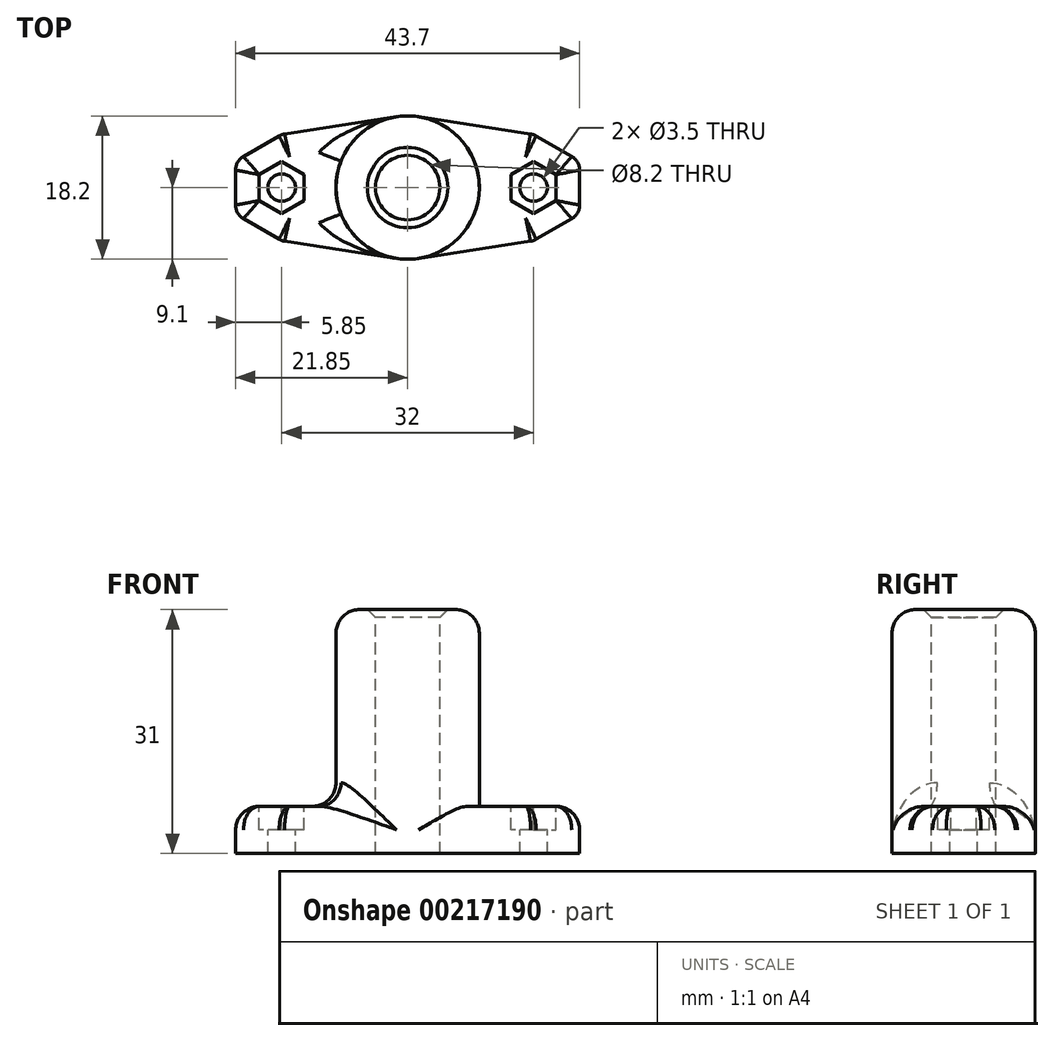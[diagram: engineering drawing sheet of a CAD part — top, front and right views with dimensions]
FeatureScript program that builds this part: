
annotation { "Feature Type Name" : "Feature", "Feature Type Description" : "" }
export const myFeature = defineFeature(function(context is Context, id is Id, definition is map)
    precondition{}
    {
        {
            var Q0;
            Q0=qCreatedBy(makeId("Top.planeOp"),FACE);
            var sketch = newSketch(context, id + "F0", { "sketchPlane" : qUnion([Q0])});
            skCircle(sketch, "E0", {"center": v(0, 0) * mm, "radius": 4.1 * mm});
            skCircle(sketch, "E1", {"center": v(-16, 0) * mm, "radius": 1.75 * mm});
            skCircle(sketch, "E2.cCircle", {"center": v(-16, 0) * mm, "radius": 2.85 * mm, "construction": true});
            skLineSegment(sketch, "E2.0", {"start": v(-18.85, -1.65) * mm, "end": v(-18.85, 1.65) * mm});
            skLineSegment(sketch, "E2.1", {"start": v(-18.85, 1.65) * mm, "end": v(-16, 3.3) * mm});
            skLineSegment(sketch, "E2.2", {"start": v(-16, 3.3) * mm, "end": v(-13.15, 1.65) * mm});
            skLineSegment(sketch, "E2.3", {"start": v(-13.15, 1.65) * mm, "end": v(-13.15, -1.65) * mm});
            skLineSegment(sketch, "E2.4", {"start": v(-13.15, -1.65) * mm, "end": v(-16, -3.3) * mm});
            skLineSegment(sketch, "E2.5", {"start": v(-16, -3.3) * mm, "end": v(-18.85, -1.65) * mm});
            skPoint(sketch, "E2.0.midPoint", {"position": v(-18.85, 0) * mm});
            skCircle(sketch, "E3.0", {"center": v(0, 0) * mm, "radius": 9.1 * mm});
            skCircle(sketch, "E4.cCircle", {"center": v(-16, 0) * mm, "radius": 5.85 * mm, "construction": true});
            skLineSegment(sketch, "E4.0", {"start": v(-21.85, -3.38) * mm, "end": v(-21.85, 3.38) * mm});
            skLineSegment(sketch, "E4.1", {"start": v(-21.85, 3.38) * mm, "end": v(-16, 6.75) * mm});
            skLineSegment(sketch, "E4.2", {"start": v(-16, 6.75) * mm, "end": v(-10.15, 3.38) * mm});
            skLineSegment(sketch, "E4.3", {"start": v(-10.15, 3.38) * mm, "end": v(-10.15, -3.38) * mm});
            skLineSegment(sketch, "E4.4", {"start": v(-10.15, -3.38) * mm, "end": v(-16, -6.75) * mm});
            skLineSegment(sketch, "E4.5", {"start": v(-16, -6.75) * mm, "end": v(-21.85, -3.38) * mm});
            skPoint(sketch, "E4.0.midPoint", {"position": v(-21.85, 0) * mm});
            skLineSegment(sketch, "E5.MirrorCS", {"start": v(10.15, -3.38) * mm, "end": v(16, -6.75) * mm});
            skPoint(sketch, "E6.MirrorP", {"position": v(18.85, 0) * mm});
            skLineSegment(sketch, "E7.MirrorCS", {"start": v(13.15, 1.65) * mm, "end": v(13.15, -1.65) * mm});
            skLineSegment(sketch, "E8.MirrorCS", {"start": v(16, -3.3) * mm, "end": v(18.85, -1.65) * mm});
            skLineSegment(sketch, "E9.MirrorCS", {"start": v(16, -6.75) * mm, "end": v(21.85, -3.38) * mm});
            skLineSegment(sketch, "E10.MirrorCS", {"start": v(16, 6.75) * mm, "end": v(10.15, 3.38) * mm});
            skCircle(sketch, "E11.MirrorC", {"center": v(16, 0) * mm, "radius": 1.75 * mm});
            skLineSegment(sketch, "E12.MirrorCS", {"start": v(21.85, 3.38) * mm, "end": v(16, 6.75) * mm});
            skLineSegment(sketch, "E13.MirrorCS", {"start": v(10.15, 3.38) * mm, "end": v(10.15, -3.38) * mm});
            skLineSegment(sketch, "E14.MirrorCS", {"start": v(21.85, -3.38) * mm, "end": v(21.85, 3.38) * mm});
            skCircle(sketch, "E15.MirrorC", {"center": v(16, 0) * mm, "radius": 5.85 * mm, "construction": true});
            skLineSegment(sketch, "E16.MirrorCS", {"start": v(13.15, -1.65) * mm, "end": v(16, -3.3) * mm});
            skLineSegment(sketch, "E17.MirrorCS", {"start": v(18.85, 1.65) * mm, "end": v(16, 3.3) * mm});
            skCircle(sketch, "E18.MirrorC", {"center": v(16, 0) * mm, "radius": 2.85 * mm, "construction": true});
            skLineSegment(sketch, "E19.MirrorCS", {"start": v(16, 3.3) * mm, "end": v(13.15, 1.65) * mm});
            skLineSegment(sketch, "E20.MirrorCS", {"start": v(18.85, -1.65) * mm, "end": v(18.85, 1.65) * mm});
            skPoint(sketch, "E21.MirrorP", {"position": v(21.85, 0) * mm});
            skLineSegment(sketch, "E22", {"start": v(-16, 6.75) * mm, "end": v(-1.38, 9) * mm});
            skLineSegment(sketch, "E23", {"start": v(16, 6.75) * mm, "end": v(1.38, 9) * mm});
            skLineSegment(sketch, "E24", {"start": v(16, -6.75) * mm, "end": v(1.38, -9) * mm});
            skLineSegment(sketch, "E25", {"start": v(-16, -6.75) * mm, "end": v(-1.38, -9) * mm});
            skSolve(sketch);
        }
        {
            var Q0;
            Q0=makeQuery(id+"F0.imprint","IMPRINT",FACE,{"disambiguationData":[TD([[makeQuery(id+"F0.imprint","IMPRINT",EDGE,{"derivedFrom":sQuery(id+"F0.wireOp",EDGE,"E2.0")}),1.0]])]});
            var Q1;
            Q1=makeQuery(id+"F0.imprint","IMPRINT",FACE,{"disambiguationData":[TD([[makeQuery(id+"F0.imprint","IMPRINT",EDGE,{"derivedFrom":sQuery(id+"F0.wireOp",EDGE,"E1")}),-1.0]])]});
            var Q2;
            Q2=makeQuery(id+"F0.imprint","IMPRINT",FACE,{"disambiguationData":[TD([[makeQuery(id+"F0.imprint","IMPRINT",EDGE,{"derivedFrom":sQuery(id+"F0.wireOp",EDGE,"E4.2")}),1.0]])]});
            var Q3;
            Q3=makeQuery(id+"F0.imprint","IMPRINT",FACE,{"disambiguationData":[TD([[makeQuery(id+"F0.imprint","IMPRINT",EDGE,{"derivedFrom":sQuery(id+"F0.wireOp",EDGE,"E0")}),-1.0]])]});
            var Q4;
            Q4=makeQuery(id+"F0.imprint","IMPRINT",FACE,{"disambiguationData":[TD([[makeQuery(id+"F0.imprint","IMPRINT",EDGE,{"derivedFrom":sQuery(id+"F0.wireOp",EDGE,"E5.MirrorCS")}),-1.0]])]});
            var Q5;
            Q5=makeQuery(id+"F0.imprint","IMPRINT",FACE,{"disambiguationData":[TD([[makeQuery(id+"F0.imprint","IMPRINT",EDGE,{"derivedFrom":sQuery(id+"F0.wireOp",EDGE,"E5.MirrorCS")}),1.0]])]});
            var Q6;
            Q6=makeQuery(id+"F0.imprint","IMPRINT",FACE,{"disambiguationData":[TD([[makeQuery(id+"F0.imprint","IMPRINT",EDGE,{"derivedFrom":sQuery(id+"F0.wireOp",EDGE,"E7.MirrorCS")}),1.0]])]});
            extrude(context, id + "F1", {"entities" : qUnion([Q0, Q1, Q2, Q3, Q4, Q5, Q6]), "oppositeDirection" : true, "depth" : 6 * mm});
        }
        {
            var Q0;
            Q0=makeQuery(id+"F0.imprint","IMPRINT",FACE,{"disambiguationData":[TD([[makeQuery(id+"F0.imprint","IMPRINT",EDGE,{"derivedFrom":sQuery(id+"F0.wireOp",EDGE,"E1")}),-1.0]])]});
            var Q1;
            Q1=makeQuery(id+"F0.imprint","IMPRINT",FACE,{"disambiguationData":[TD([[makeQuery(id+"F0.imprint","IMPRINT",EDGE,{"derivedFrom":sQuery(id+"F0.wireOp",EDGE,"E7.MirrorCS")}),1.0]])]});
            extrude(context, id + "F2", {"entities" : qUnion([Q0, Q1]), "operationType" : NewBodyOperationType.REMOVE, "oppositeDirection" : true, "depth" : 3 * mm});
        }
        {
            var Q0;
            Q0=makeQuery(id+"F0.imprint","IMPRINT",FACE,{"disambiguationData":[TD([[makeQuery(id+"F0.imprint","IMPRINT",EDGE,{"derivedFrom":sQuery(id+"F0.wireOp",EDGE,"E0")}),-1.0]])]});
            extrude(context, id + "F3", {"entities" : qUnion([Q0]), "operationType" : NewBodyOperationType.ADD, "depth" : 25 * mm});
        }
        {
            var Q0;
            Q0=makeQuery(id+"F1.opExtrude","CAP_EDGE",EDGE,{"disambiguationData":[OSD([sQuery(id+"F0.wireOp",EDGE,"E25")])],"isStart":true});
            var Q1;
            Q1=makeQuery(id+"F1.opExtrude","CAP_EDGE",EDGE,{"disambiguationData":[OSD([sQuery(id+"F0.wireOp",EDGE,"E4.5")])],"isStart":true});
            var Q2;
            Q2=makeQuery(id+"F1.opExtrude","CAP_EDGE",EDGE,{"disambiguationData":[OSD([sQuery(id+"F0.wireOp",EDGE,"E4.0")])],"isStart":true});
            var Q3;
            Q3=makeQuery(id+"F1.opExtrude","CAP_EDGE",EDGE,{"disambiguationData":[OSD([sQuery(id+"F0.wireOp",EDGE,"E4.1")])],"isStart":true});
            var Q4;
            Q4=makeQuery(id+"F1.opExtrude","CAP_EDGE",EDGE,{"disambiguationData":[OSD([sQuery(id+"F0.wireOp",EDGE,"E22")])],"isStart":true});
            var Q5;
            Q5=makeQuery(id+"F1.opExtrude","CAP_EDGE",EDGE,{"disambiguationData":[OSD([sQuery(id+"F0.wireOp",EDGE,"E23")])],"isStart":true});
            var Q6;
            Q6=makeQuery(id+"F1.opExtrude","CAP_EDGE",EDGE,{"disambiguationData":[OSD([sQuery(id+"F0.wireOp",EDGE,"E12.MirrorCS")])],"isStart":true});
            var Q7;
            Q7=makeQuery(id+"F1.opExtrude","CAP_EDGE",EDGE,{"disambiguationData":[OSD([sQuery(id+"F0.wireOp",EDGE,"E14.MirrorCS")])],"isStart":true});
            var Q8;
            Q8=makeQuery(id+"F1.opExtrude","CAP_EDGE",EDGE,{"disambiguationData":[OSD([sQuery(id+"F0.wireOp",EDGE,"E9.MirrorCS")])],"isStart":true});
            var Q9;
            Q9=makeQuery(id+"F1.opExtrude","CAP_EDGE",EDGE,{"disambiguationData":[OSD([sQuery(id+"F0.wireOp",EDGE,"E24")])],"isStart":true});
            var Q10;
            Q10=makeQuery(id+"F3.opExtrude","CAP_EDGE",EDGE,{"disambiguationData":[OSD([sQuery(id+"F0.wireOp",EDGE,"E3.0")])],"isStart":false});
            var Q11;
            {var subQ0=sQuery(id+"F0.wireOp",EDGE,"E22");var subQ2=sQuery(id+"F0.wireOp",EDGE,"E3.0");Q11=makeQuery(id+"F3.boolean.opBoolean","SPLIT",EDGE,{"disambiguationData":[TD([makeQuery(id+"F1.opExtrude","SWEPT_FACE",FACE,{"disambiguationData":[OSD([subQ0])]})])],"derivedFrom":makeQuery(id+"F3.opExtrude","CAP_EDGE",EDGE,{"disambiguationData":[OSD([subQ2])],"isStart":true})});}
            var Q12;
            {var subQ1=sQuery(id+"F0.wireOp",EDGE,"E3.0");var subQ4=sQuery(id+"F0.wireOp",EDGE,"E23");Q12=makeQuery(id+"F3.boolean.opBoolean","SPLIT",EDGE,{"disambiguationData":[TD([makeQuery(id+"F1.opExtrude","SWEPT_FACE",FACE,{"disambiguationData":[OSD([subQ4])]})])],"derivedFrom":makeQuery(id+"F3.opExtrude","CAP_EDGE",EDGE,{"disambiguationData":[OSD([subQ1])],"isStart":true})});}
            fillet(context, id + "F4", {"entities" : qUnion([Q0, Q1, Q2, Q3, Q4, Q5, Q6, Q7, Q8, Q9, Q10, Q11, Q12]), "radius" : 3 * mm, "tangentPropagation" : true, "allowEdgeOverflow" : false});
        }
        {
            var Q0;
            Q0=makeQuery(id+"F3.opExtrude","CAP_EDGE",EDGE,{"disambiguationData":[OSD([sQuery(id+"F0.wireOp",EDGE,"E0")])],"isStart":false});
            chamfer(context, id + "F5", {"entities" : qUnion([Q0]), "width" : 1 * mm, "tangentPropagation" : true});
        }
        {
            var Q0;
            Q0=makeQuery(id+"F4.opFillet","BLEND_EDGE",EDGE,{"blendedFrom":[makeQuery(id+"F1.opExtrude","CAP_EDGE",EDGE,{"disambiguationData":[OSD([sQuery(id+"F0.wireOp",EDGE,"E12.MirrorCS")])],"isStart":true}),makeQuery(id+"F1.opExtrude","CAP_EDGE",EDGE,{"disambiguationData":[OSD([sQuery(id+"F0.wireOp",EDGE,"E14.MirrorCS")])],"isStart":true})],"blendedInto":[]});
            var Q1;
            Q1=makeQuery(id+"F4.opFillet","BLEND_EDGE",EDGE,{"blendedFrom":[makeQuery(id+"F1.opExtrude","CAP_EDGE",EDGE,{"disambiguationData":[OSD([sQuery(id+"F0.wireOp",EDGE,"E12.MirrorCS")])],"isStart":true}),makeQuery(id+"F1.opExtrude","CAP_EDGE",EDGE,{"disambiguationData":[OSD([sQuery(id+"F0.wireOp",EDGE,"E23")])],"isStart":true})],"blendedInto":[]});
            var Q2;
            Q2=makeQuery(id+"F4.opFillet","BLEND_EDGE",EDGE,{"blendedFrom":[makeQuery(id+"F1.opExtrude","CAP_EDGE",EDGE,{"disambiguationData":[OSD([sQuery(id+"F0.wireOp",EDGE,"E9.MirrorCS")])],"isStart":true}),makeQuery(id+"F1.opExtrude","CAP_EDGE",EDGE,{"disambiguationData":[OSD([sQuery(id+"F0.wireOp",EDGE,"E14.MirrorCS")])],"isStart":true})],"blendedInto":[]});
            var Q3;
            Q3=makeQuery(id+"F4.opFillet","BLEND_EDGE",EDGE,{"blendedFrom":[makeQuery(id+"F1.opExtrude","CAP_EDGE",EDGE,{"disambiguationData":[OSD([sQuery(id+"F0.wireOp",EDGE,"E9.MirrorCS")])],"isStart":true}),makeQuery(id+"F1.opExtrude","CAP_EDGE",EDGE,{"disambiguationData":[OSD([sQuery(id+"F0.wireOp",EDGE,"E24")])],"isStart":true})],"blendedInto":[]});
            var Q4;
            Q4=makeQuery(id+"F4.opFillet","BLEND_EDGE",EDGE,{"blendedFrom":[makeQuery(id+"F1.opExtrude","CAP_EDGE",EDGE,{"disambiguationData":[OSD([sQuery(id+"F0.wireOp",EDGE,"E4.1")])],"isStart":true}),makeQuery(id+"F1.opExtrude","CAP_EDGE",EDGE,{"disambiguationData":[OSD([sQuery(id+"F0.wireOp",EDGE,"E22")])],"isStart":true})],"blendedInto":[]});
            var Q5;
            Q5=makeQuery(id+"F4.opFillet","BLEND_EDGE",EDGE,{"blendedFrom":[makeQuery(id+"F1.opExtrude","CAP_EDGE",EDGE,{"disambiguationData":[OSD([sQuery(id+"F0.wireOp",EDGE,"E4.0")])],"isStart":true}),makeQuery(id+"F1.opExtrude","CAP_EDGE",EDGE,{"disambiguationData":[OSD([sQuery(id+"F0.wireOp",EDGE,"E4.1")])],"isStart":true})],"blendedInto":[]});
            var Q6;
            Q6=makeQuery(id+"F4.opFillet","BLEND_EDGE",EDGE,{"blendedFrom":[makeQuery(id+"F1.opExtrude","CAP_EDGE",EDGE,{"disambiguationData":[OSD([sQuery(id+"F0.wireOp",EDGE,"E4.0")])],"isStart":true}),makeQuery(id+"F1.opExtrude","CAP_EDGE",EDGE,{"disambiguationData":[OSD([sQuery(id+"F0.wireOp",EDGE,"E4.5")])],"isStart":true})],"blendedInto":[]});
            var Q7;
            Q7=makeQuery(id+"F4.opFillet","BLEND_EDGE",EDGE,{"blendedFrom":[makeQuery(id+"F1.opExtrude","CAP_EDGE",EDGE,{"disambiguationData":[OSD([sQuery(id+"F0.wireOp",EDGE,"E4.5")])],"isStart":true}),makeQuery(id+"F1.opExtrude","CAP_EDGE",EDGE,{"disambiguationData":[OSD([sQuery(id+"F0.wireOp",EDGE,"E25")])],"isStart":true})],"blendedInto":[]});
            fillet(context, id + "F6", {"entities" : qUnion([Q0, Q1, Q2, Q3, Q4, Q5, Q6, Q7]), "radius" : 2 * mm, "tangentPropagation" : true, "allowEdgeOverflow" : false});
        }
    });
